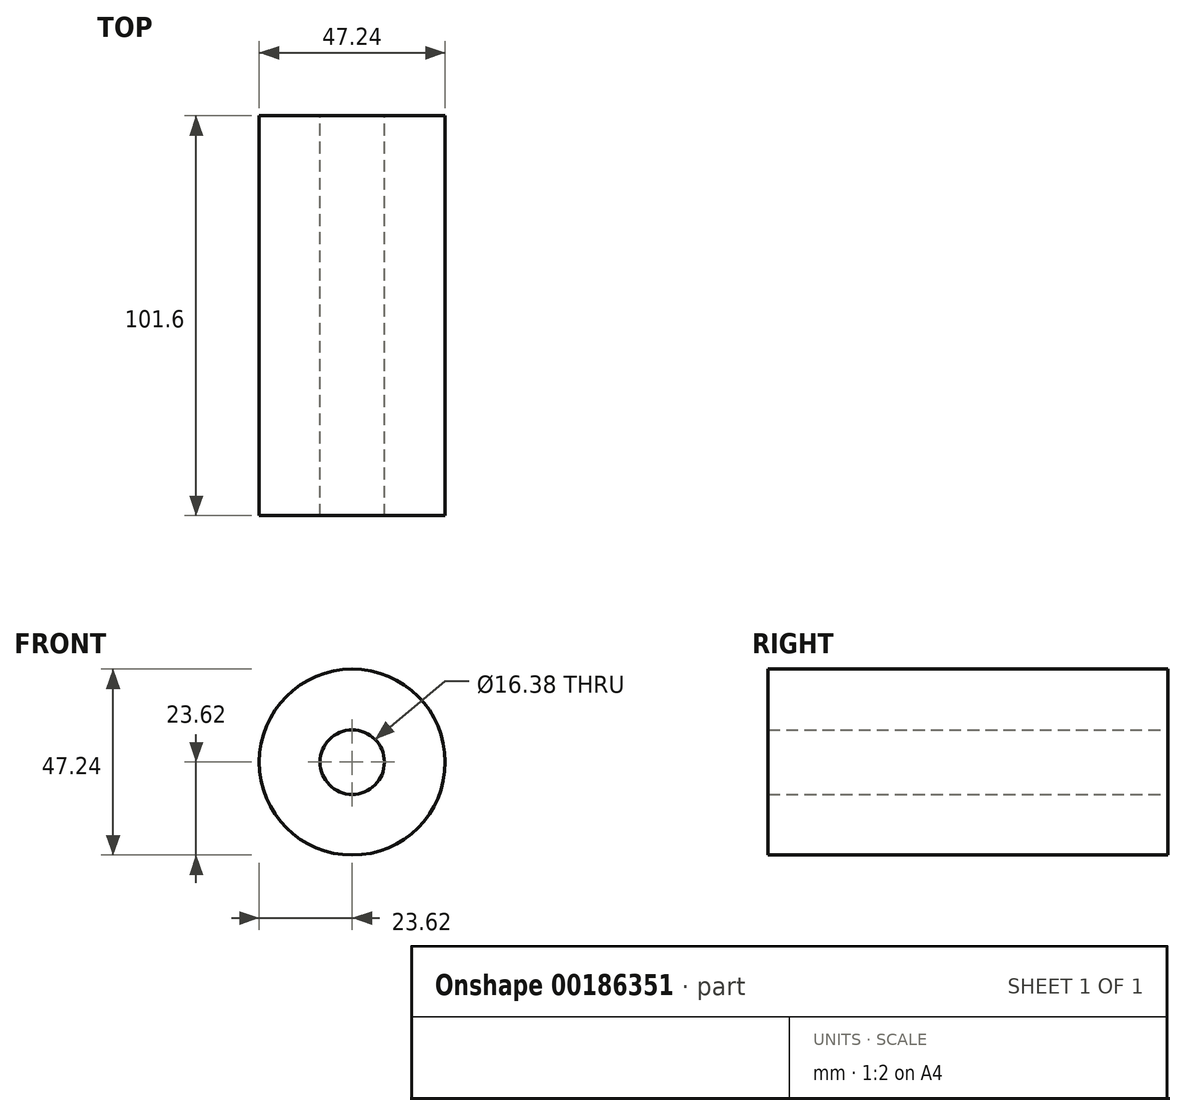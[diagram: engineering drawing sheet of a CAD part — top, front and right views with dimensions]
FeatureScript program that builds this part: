
annotation { "Feature Type Name" : "Feature", "Feature Type Description" : "" }
export const myFeature = defineFeature(function(context is Context, id is Id, definition is map)
    precondition{}
    {
        {
            var Q0;
            Q0=qCreatedBy(makeId("Front.planeOp"),FACE);
            var sketch = newSketch(context, id + "F0", { "sketchPlane" : qUnion([Q0])});
            skCircle(sketch, "E0", {"center": v(0, 0) * mm, "radius": 23.62 * mm});
            skCircle(sketch, "E1", {"center": v(0, 0) * mm, "radius": 8.19 * mm});
            skSolve(sketch);
        }
        {
            var Q0;
            Q0=makeQuery(id+"F0.imprint","IMPRINT",FACE,{"disambiguationData":[TD([[makeQuery(id+"F0.imprint","IMPRINT",EDGE,{"derivedFrom":sQuery(id+"F0.wireOp",EDGE,"E0")}),1.0]])]});
            extrude(context, id + "F1", {"entities" : qUnion([Q0]), "depth" : 50.8 * mm, "hasSecondDirection" : true, "secondDirectionOppositeDirection" : true, "secondDirectionDepth" : 50.8 * mm});
        }
        {
            var Q0;
            Q0=qCreatedBy(makeId("Front.planeOp"),FACE);
            var sketch = newSketch(context, id + "F2", { "sketchPlane" : qUnion([Q0])});
            skCircle(sketch, "E2", {"center": v(44.11, -20) * mm, "radius": 28.9 * mm});
            skCircle(sketch, "E3", {"center": v(-6.8, 47.03) * mm, "radius": 28.9 * mm});
            skCircle(sketch, "E4", {"center": v(-38.45, -28.22) * mm, "radius": 28.9 * mm});
            skSolve(sketch);
        }
        {
            var Q0;
            Q0=sQuery(id+"F2.wireOp",EDGE,"E4");
            extrude(context, id + "F3", {"bodyType" : ToolBodyType.SURFACE, "surfaceEntities" : qUnion([Q0]), "depth" : 25.4 * mm});
        }
    });
